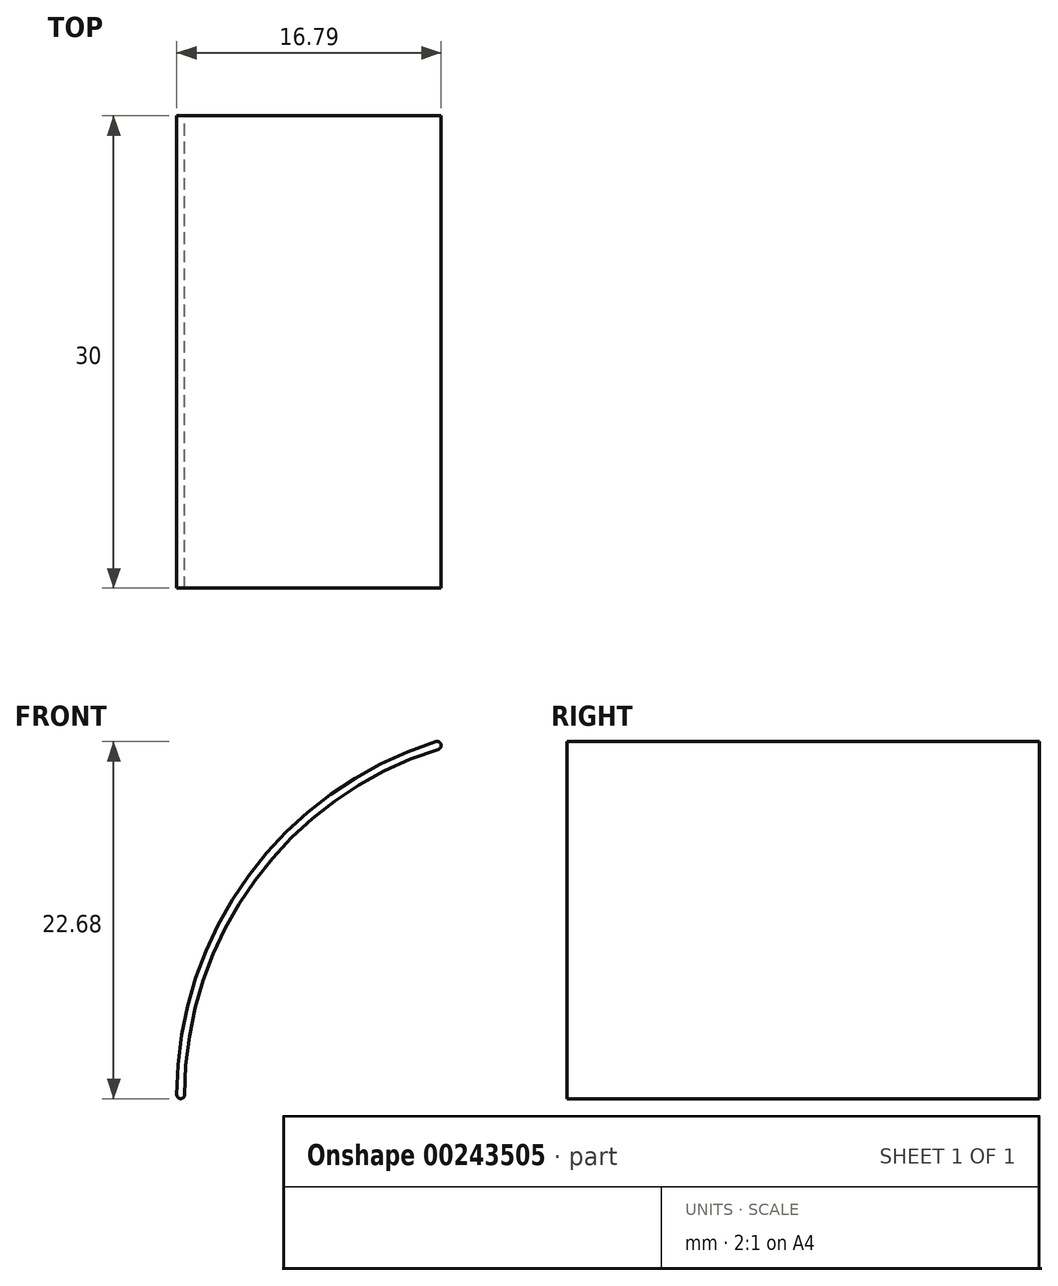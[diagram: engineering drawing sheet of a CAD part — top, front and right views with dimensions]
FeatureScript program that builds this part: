
annotation { "Feature Type Name" : "Feature", "Feature Type Description" : "" }
export const myFeature = defineFeature(function(context is Context, id is Id, definition is map)
    precondition{}
    {
        {
            var Q0;
            Q0=qCreatedBy(makeId("Front.planeOp"),FACE);
            var sketch = newSketch(context, id + "F0", { "sketchPlane" : qUnion([Q0])});
            skArc(sketch, "E0", {"start": v(-6.88, 21.95) * mm, "mid": v(-18.54, 13.61) * mm, "end": v(-23, 0) * mm});
            skArc(sketch, "E1", {"start": v(-7.03, 22.42) * mm, "mid": v(-18.94, 13.91) * mm, "end": v(-23.5, 0) * mm});
            skArc(sketch, "E2", {"start": v(-23.5, 0) * mm, "mid": v(-23.25, -0.25) * mm, "end": v(-23, 0) * mm});
            skArc(sketch, "E3", {"start": v(-6.88, 21.95) * mm, "mid": v(-6.72, 22.26) * mm, "end": v(-7.03, 22.42) * mm});
            skSolve(sketch);
        }
        {
            var Q0;
            Q0=makeQuery(id+"F0.imprint","IMPRINT",FACE,{"disambiguationData":[TD([[makeQuery(id+"F0.imprint","IMPRINT",EDGE,{"derivedFrom":sQuery(id+"F0.wireOp",EDGE,"E0")}),-1.0]])]});
            extrude(context, id + "F1", {"entities" : qUnion([Q0]), "depth" : 30 * mm});
        }
    });
